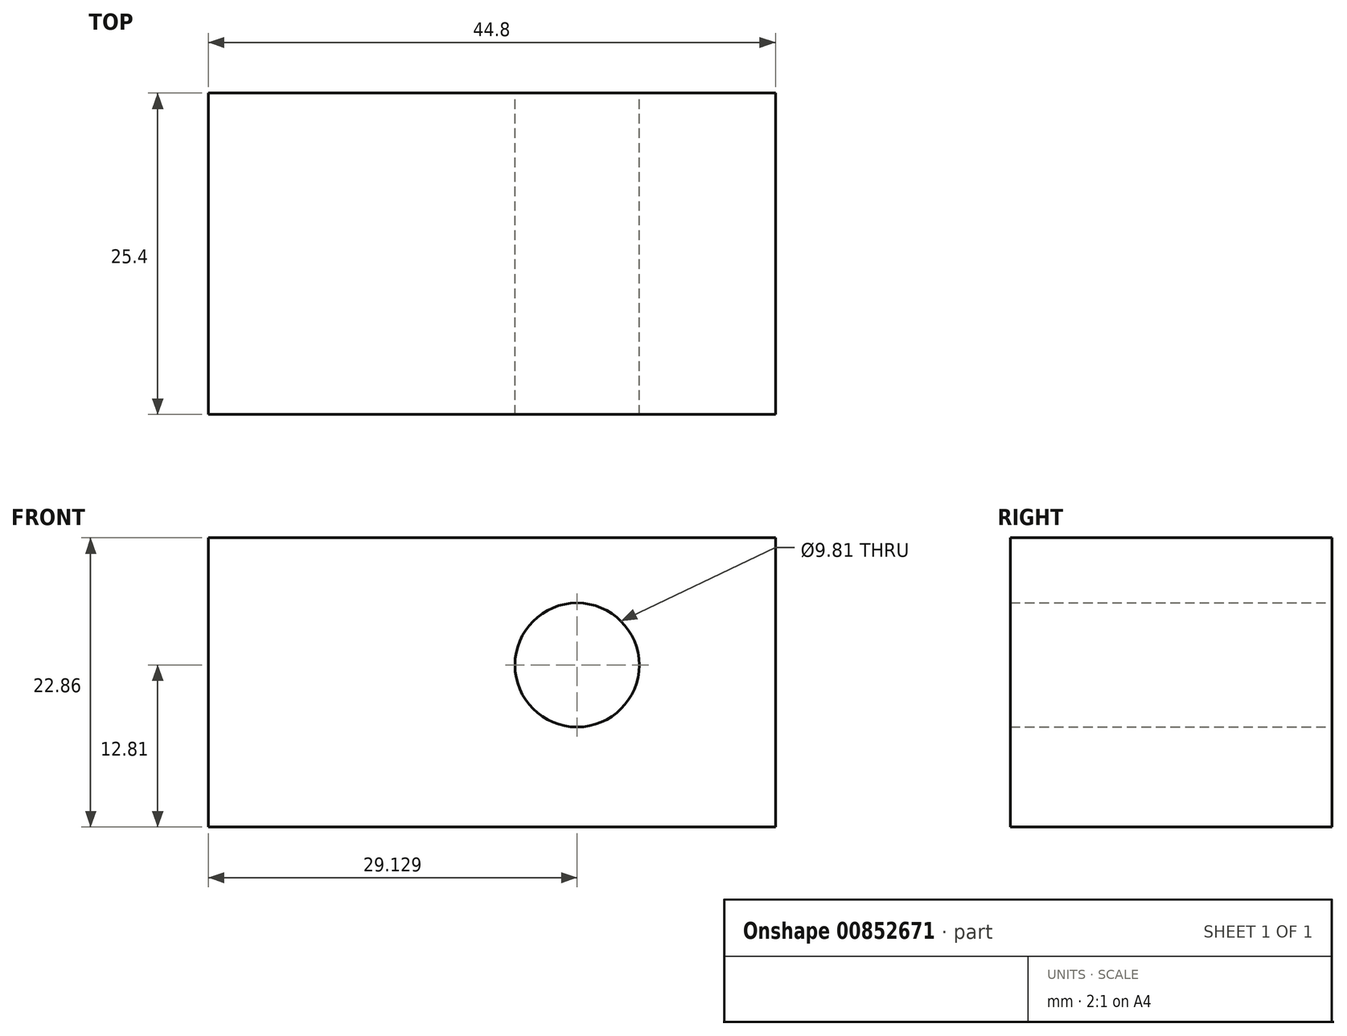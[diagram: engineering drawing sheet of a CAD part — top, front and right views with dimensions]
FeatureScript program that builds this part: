
annotation { "Feature Type Name" : "Feature", "Feature Type Description" : "" }
export const myFeature = defineFeature(function(context is Context, id is Id, definition is map)
    precondition{}
    {
        {
            var Q0;
            Q0=qCreatedBy(makeId("Front.planeOp"),FACE);
            var sketch = newSketch(context, id + "F0", { "sketchPlane" : qUnion([Q0])});
            skLineSegment(sketch, "E0.bottom", {"start": v(-13.92, 10.05) * mm, "end": v(30.88, 10.05) * mm});
            skLineSegment(sketch, "E0.top", {"start": v(-13.92, -12.81) * mm, "end": v(30.88, -12.81) * mm});
            skLineSegment(sketch, "E0.left", {"start": v(-13.92, 10.05) * mm, "end": v(-13.92, -12.81) * mm});
            skLineSegment(sketch, "E0.right", {"start": v(30.88, 10.05) * mm, "end": v(30.88, -12.81) * mm});
            skCircle(sketch, "E1", {"center": v(15.2, 0) * mm, "radius": 4.9 * mm});
            skSolve(sketch);
        }
        {
            var Q0;
            Q0=makeQuery(id+"F0.imprint","IMPRINT",FACE,{"disambiguationData":[TD([[makeQuery(id+"F0.imprint","IMPRINT",EDGE,{"derivedFrom":sQuery(id+"F0.wireOp",EDGE,"E0.bottom")}),-1.0]])]});
            extrude(context, id + "F1", {"entities" : qUnion([Q0]), "depth" : 25.4 * mm, "offsetDistance" : 25.4 * mm});
        }
    });
